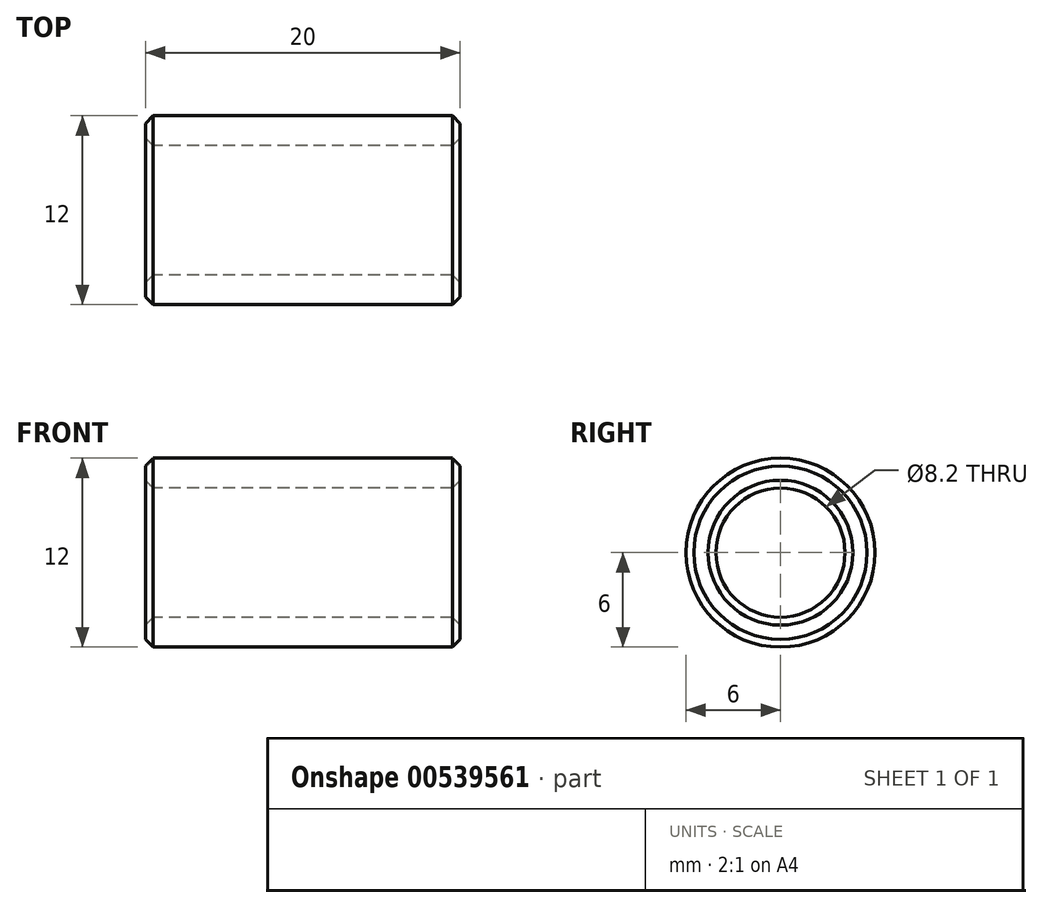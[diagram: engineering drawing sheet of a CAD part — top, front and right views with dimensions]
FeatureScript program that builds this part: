
annotation { "Feature Type Name" : "Feature", "Feature Type Description" : "" }
export const myFeature = defineFeature(function(context is Context, id is Id, definition is map)
    precondition{}
    {
        {
            var Q0;
            Q0=qCreatedBy(makeId("Front.planeOp"),FACE);
            var sketch = newSketch(context, id + "F0", { "sketchPlane" : qUnion([Q0])});
            skLineSegment(sketch, "E0.bottom", {"start": v(0, 4.1) * mm, "end": v(20, 4.1) * mm});
            skLineSegment(sketch, "E0.top", {"start": v(0, 6) * mm, "end": v(20, 6) * mm});
            skLineSegment(sketch, "E0.left", {"start": v(0, 4.1) * mm, "end": v(0, 6) * mm});
            skLineSegment(sketch, "E0.right", {"start": v(20, 4.1) * mm, "end": v(20, 6) * mm});
            skLineSegment(sketch, "E1", {"start": v(0, 0) * mm, "end": v(34.33, 0) * mm, "construction": true});
            skSolve(sketch);
        }
        {
            var Q0;
            Q0=makeQuery(id+"F0.imprint","IMPRINT",FACE,{"disambiguationData":[TD([[makeQuery(id+"F0.imprint","IMPRINT",EDGE,{"derivedFrom":sQuery(id+"F0.wireOp",EDGE,"E0.bottom")}),1.0]])]});
            var Q1;
            Q1=sQuery(id+"F0.wireOp",EDGE,"E1");
            revolve(context, id + "F1", {"surfaceOperationType" : NewSurfaceOperationType.NEW, "entities" : qUnion([Q0]), "axis" : qUnion([Q1]), "revolveType" : RevolveType.FULL});
        }
        {
            var Q0;
            Q0=makeQuery(id+"F1.opRevolve","SWEPT_EDGE",EDGE,{"disambiguationData":[OSD([sQuery(id+"F0.wireOp",EDGE,"E0.top"),sQuery(id+"F0.wireOp",EDGE,"E0.left")])]});
            var Q1;
            Q1=makeQuery(id+"F1.opRevolve","SWEPT_EDGE",EDGE,{"disambiguationData":[OSD([sQuery(id+"F0.wireOp",EDGE,"E0.top"),sQuery(id+"F0.wireOp",EDGE,"E0.right")])]});
            var Q2;
            Q2=makeQuery(id+"F1.opRevolve","SWEPT_EDGE",EDGE,{"disambiguationData":[OSD([sQuery(id+"F0.wireOp",EDGE,"E0.bottom"),sQuery(id+"F0.wireOp",EDGE,"E0.right")])]});
            var Q3;
            Q3=makeQuery(id+"F1.opRevolve","SWEPT_EDGE",EDGE,{"disambiguationData":[OSD([sQuery(id+"F0.wireOp",EDGE,"E0.bottom"),sQuery(id+"F0.wireOp",EDGE,"E0.left")])]});
            chamfer(context, id + "F2", {"entities" : qUnion([Q0, Q1, Q2, Q3]), "width" : 0.5 * mm, "tangentPropagation" : true});
        }
    });
